# Revit family: EVAN WBC
name_source: partatom
category: Оборудование
units: mm (PartAtom-declared; Revit-internal decimal feet)

## family parameters
Всегда вертикально = Да
Классификация = Нет
На основе рабочей плоскости = Нет
Общий = Нет
При загрузке вырезать с полостями = Нет
Размер круглого соединителя = Использовать диаметр
Тип детали = Нормальный
Точка расчета площади = Нет

## types (13) — shared parameters
ADSK_Классификация нагрузок = Прочее
ADSK_Количество фаз = 1
ADSK_Коэффициент мощности = 1
ADSK_Материал = Конструкционная сталь с эмалевым покрытием
ADSK_Напряжение = 0 В
ADSK_Номинальная мощность = 0 Вт
ADSK_Полная мощность = 0 кВт
ADSK_Расход ГВ = 0.0 л/с
ADSK_Расход ХВ = 0.0 л/с
Dкороба = 20 мм
G1int = 30 мм
G2int = 24 мм
URL = https://www.evan.ru
База = Бойлер косвенного нагрева напольный
В1 = 70 мм
Высота 1 = 20 мм
Материал корпуса = Конструкционная сталь с эмалевым покрытием
Напряжение питания для ТЭНа, В = 0 В
Пластик прозрачный = Пластик_прозрачный
Пластик_красный = Пластик_красный
Пластик_синий = Пластик_синий
Пластмасса_черная = Пластмасса_черная
Серый = Серый
Стекло = Стекло
Частота тока для ТЭНа, Гц = 0 Гц
Электрическая мощность ТЭНа N, кВт2) = 0 Вт

## per-type parameters (varying)
| type | D2_colp | DN1 | DN2 | Dбойлера | G1ext | G2ext | H10 | H3 | H5 | H6 | H7 | H8 | H9 | Диаметр1 | Диаметр2 | Мощность 1 змеевика, кВт | Мощность 2 змеевика, кВт | Объем, л | Площадь 2 змеевика, м2 |
| EVAN WBC 160 л. с двумя змеевиками | 27 мм | 25 мм | 20 мм | 590 мм | 31 мм | 26 мм | 857 мм | 442 мм | 662 мм | 862 мм | 940 мм | 302 мм | 612 мм | 286 мм | 289 мм | 18 кВт | 15 кВт | 173 | 0.55 м² |
| EVAN WBC 200 л. с двумя змеевиками | 27 мм | 25 мм | 20 мм | 590 мм | 31 мм | 26 мм | 1102 мм | 542 мм | 782 мм | 1042 мм | 1102 мм | 302 мм | 727 мм | 286 мм | 289 мм | 27 кВт | 18 кВт | 208 | 0.66 м² |
| EVAN WBC 300 л. с двумя змеевиками | 33 мм | 25 мм | 25 мм | 590 мм | 31 мм | 31 мм | 1617 мм | 672 мм | 912 мм | 1172 мм | 1617 мм | 312 мм | 852 мм | 286 мм | 289 мм | 36 кВт | 18 кВт | 284 | 0.66 м² |
| EVAN WBC 400 л. с двумя змеевиками | 33 мм | 25 мм | 25 мм | 750 мм | 31 мм | 31 мм | 1142 мм | 577 мм | 816 мм | 1016 мм | 1142 мм | 337 мм | 757 мм | 366 мм | 369 мм | 43 кВт | 22 кВт | 409 | 0.8 м² |
| EVAN WBC 500 л. с двумя змеевиками | 33 мм | 25 мм | 25 мм | 750 мм | 31 мм | 31 мм | 1385 мм | 765 мм | 975 мм | 1335 мм | 1405 мм | 330 мм | 930 мм | 366 мм | 369 мм | 53 кВт | 37 кВт | 510 | 1.37 м² |
| EVAN WBC 800 л. с двумя змеевиками | 40 мм | 32 мм | 32 мм | 950 мм | 38 мм | 38 мм | 1366 мм | 841 мм | 1081 мм | 1301 мм | 1456 мм | 411 мм | 1021 мм | 466 мм | 469 мм | 69 кВт | 27 кВт | 814 | 1.02 м² |
| EVAN WBC 1000 л. с двумя змеевиками | 40 мм | 32 мм | 32 мм | 950 мм | 38 мм | 38 мм | 1697 мм | 923 мм | 1163 мм | 1492 мм | 1697 мм | 393 мм | 1103 мм | 466 мм | 469 мм | 82 кВт | 41 кВт | 1004 | 1.53 м² |
| EVAN WBC 1500 л. с двумя змеевиками | 40 мм | 32 мм | 32 мм | 1120 мм | 38 мм | 38 мм | 1950 мм | 995 мм | 1235 мм | 1565 мм | 1950 мм | 395 мм | 1175 мм | 551 мм | 554 мм | 108 кВт | 50 кВт | 1463 | 1.86 м² |
| EVAN WBC 2000 л. с двумя змеевиками | 40 мм | 32 мм | 32 мм | 1260 мм | 38 мм | 38 мм | 1954 мм | 999 мм | 1239 мм | 1569 мм | 1954 мм | 399 мм | 1179 мм | 621 мм | 624 мм | 126 кВт | 58 кВт | 1811 | 2.16 м² |
| EVAN WBC 2500 л. с двумя змеевиками | 48 мм | 32 мм | 40 мм | 1460 мм | 38 мм | 46 мм | 1807 мм | 1104 мм | 1324 мм | 1819 мм | 1914 мм | 504 мм | 1272 мм | 721 мм | 724 мм | 148 кВт | 102 кВт | 2325 | 3.8 м² |
| EVAN WBC 3000 л. с двумя змеевиками | 48 мм | 32 мм | 40 мм | 1460 мм | 38 мм | 46 мм | 2309 мм | 1264 мм | 1504 мм | 2004 мм | 2309 мм | 504 мм | 1504 мм | 721 мм | 724 мм | 182 кВт | 102 кВт | 2785 | 3.8 м² |
| EVAN WBC 4000 л. с двумя змеевиками | 48 мм | 50 мм | 40 мм | 1710 мм | 56 мм | 46 мм | 2039 мм | 1294 мм | 1534 мм | 2034 мм | 2161 мм | 534 мм | 1474 мм | 846 мм | 849 мм | 218 кВт | 122 кВт | 4000 | 4.55 м² |
| EVAN WBC 5000 л. с двумя змеевиками | 48 мм | 50 мм | 40 мм | 1710 мм | 56 мм | 46 мм | 2533 мм | 1508 мм | 1748 мм | 2398 мм | 2533 мм | 528 мм | 1688 мм | 846 мм | 849 мм | 258 кВт | 163 кВт | 5000 | 6.07 м² |
